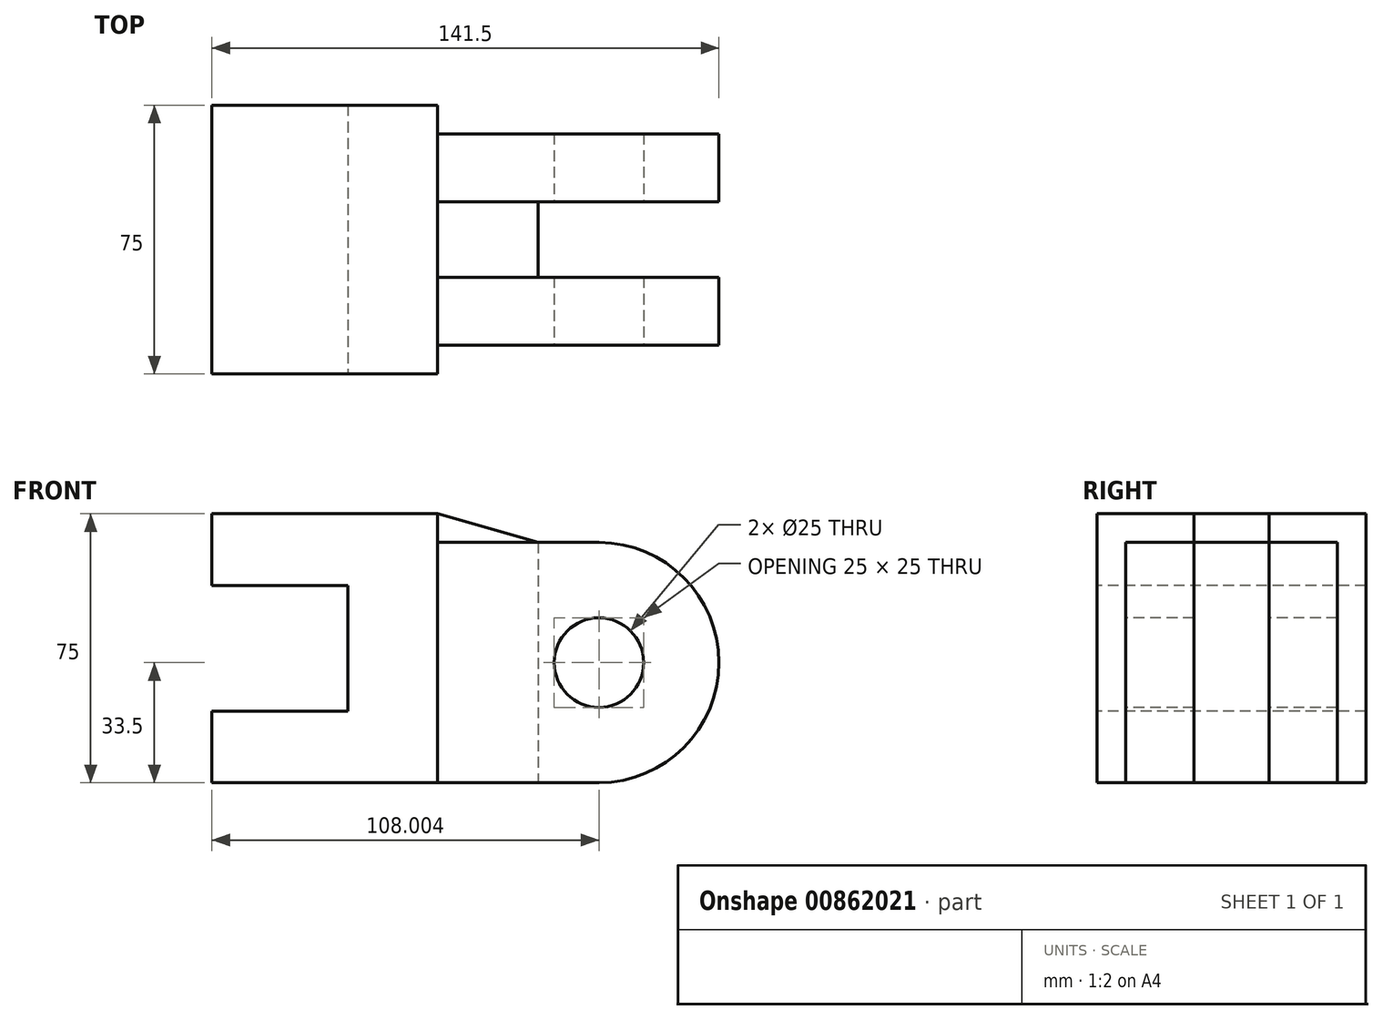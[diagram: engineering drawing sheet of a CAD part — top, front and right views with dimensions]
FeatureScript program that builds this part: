
annotation { "Feature Type Name" : "Feature", "Feature Type Description" : "" }
export const myFeature = defineFeature(function(context is Context, id is Id, definition is map)
    precondition{}
    {
        {
            var Q0;
            Q0=qCreatedBy(makeId("Top.planeOp"),FACE);
            var sketch = newSketch(context, id + "F0", { "sketchPlane" : qUnion([Q0])});
            skLineSegment(sketch, "E0.bottom", {"start": v(-50.72, 36.49) * mm, "end": v(12.28, 36.49) * mm});
            skLineSegment(sketch, "E0.top", {"start": v(-50.72, -38.51) * mm, "end": v(12.28, -38.51) * mm});
            skLineSegment(sketch, "E0.left", {"start": v(-50.72, 36.49) * mm, "end": v(-50.72, -38.51) * mm});
            skLineSegment(sketch, "E0.right", {"start": v(12.28, 36.49) * mm, "end": v(12.28, -38.51) * mm});
            skSolve(sketch);
        }
        {
            var Q0;
            Q0=qSketchRegion(id+"F0",true);
            extrude(context, id + "F1", {"entities" : qUnion([Q0]), "depth" : 75 * mm, "offsetDistance" : 25 * mm});
        }
        {
            var Q0;
            Q0=makeQuery(id+"F1.opExtrude","SWEPT_FACE",FACE,{"disambiguationData":[OSD([sQuery(id+"F0.wireOp",EDGE,"E0.top")])]});
            var sketch = newSketch(context, id + "F2", { "sketchPlane" : qUnion([Q0])});
            skLineSegment(sketch, "E1", {"start": v(-50.72, 0) * mm, "end": v(-50.72, 20) * mm});
            skLineSegment(sketch, "E2", {"start": v(-50.72, 20) * mm, "end": v(-12.72, 20) * mm});
            skLineSegment(sketch, "E3", {"start": v(-12.72, 20) * mm, "end": v(-12.72, 55) * mm});
            skLineSegment(sketch, "E4", {"start": v(-12.72, 55) * mm, "end": v(-50.72, 55) * mm});
            skLineSegment(sketch, "E5", {"start": v(-50.72, 55) * mm, "end": v(-50.72, 75) * mm});
            skSolve(sketch);
        }
        {
            var Q0;
            {var subQ0=sQuery(id+"F2.wireOp",EDGE,"E2");Q0=makeQuery(id+"F2.imprint","IMPRINT",FACE,{"disambiguationData":[TD([[makeQuery(id+"F2.imprint","IMPRINT",EDGE,{"derivedFrom":subQ0}),1.0]])]});}
            extrude(context, id + "F3", {"entities" : qUnion([Q0]), "operationType" : NewBodyOperationType.REMOVE, "oppositeDirection" : true, "depth" : 75 * mm, "offsetDistance" : 25 * mm});
        }
        {
            var Q0;
            Q0=makeQuery(id+"F1.opExtrude","SWEPT_FACE",FACE,{"disambiguationData":[OSD([sQuery(id+"F0.wireOp",EDGE,"E0.right")])]});
            var sketch = newSketch(context, id + "F4", { "sketchPlane" : qUnion([Q0])});
            skLineSegment(sketch, "E6", {"start": v(-30.51, 67) * mm, "end": v(-30.51, 0) * mm});
            skLineSegment(sketch, "E7", {"start": v(-30.51, 0) * mm, "end": v(-11.51, 0) * mm});
            skLineSegment(sketch, "E8", {"start": v(-11.51, 0) * mm, "end": v(9.49, 0) * mm});
            skLineSegment(sketch, "E9", {"start": v(9.49, 0) * mm, "end": v(28.49, 0) * mm});
            skLineSegment(sketch, "E10", {"start": v(28.49, 0) * mm, "end": v(28.49, 67) * mm});
            skLineSegment(sketch, "E11", {"start": v(28.49, 67) * mm, "end": v(9.49, 67) * mm});
            skLineSegment(sketch, "E12", {"start": v(9.49, 67) * mm, "end": v(9.49, 0) * mm});
            skLineSegment(sketch, "E13", {"start": v(-30.51, 67) * mm, "end": v(-11.51, 67) * mm});
            skLineSegment(sketch, "E14", {"start": v(-11.51, 67) * mm, "end": v(-11.51, 0) * mm});
            skLineSegment(sketch, "E15", {"start": v(-11.51, 67) * mm, "end": v(-11.51, 75) * mm});
            skLineSegment(sketch, "E16", {"start": v(-11.51, 75) * mm, "end": v(9.49, 75) * mm});
            skLineSegment(sketch, "E17", {"start": v(9.49, 75) * mm, "end": v(9.49, 67) * mm});
            skSolve(sketch);
        }
        {
            var Q0;
            Q0=makeQuery(id+"F4.imprint","IMPRINT",FACE,{"disambiguationData":[TD([[makeQuery(id+"F4.imprint","IMPRINT",EDGE,{"derivedFrom":sQuery(id+"F4.wireOp",EDGE,"E6")}),1.0]])]});
            var Q1;
            Q1=makeQuery(id+"F4.imprint","IMPRINT",FACE,{"disambiguationData":[TD([[makeQuery(id+"F4.imprint","IMPRINT",EDGE,{"derivedFrom":sQuery(id+"F4.wireOp",EDGE,"E9")}),-1.0]])]});
            extrude(context, id + "F5", {"entities" : qUnion([Q0, Q1]), "operationType" : NewBodyOperationType.ADD, "depth" : 45 * mm, "offsetDistance" : 25 * mm});
        }
        {
            var Q0;
            Q0=makeQuery(id+"F1.opExtrude","SWEPT_FACE",FACE,{"disambiguationData":[OSD([sQuery(id+"F0.wireOp",EDGE,"E0.right")])]});
            var sketch = newSketch(context, id + "F6", { "sketchPlane" : qUnion([Q0])});
            skLineSegment(sketch, "E18", {"start": v(-11.51, 67) * mm, "end": v(-11.51, 75) * mm});
            skLineSegment(sketch, "E19", {"start": v(-11.51, 75) * mm, "end": v(9.49, 75) * mm});
            skLineSegment(sketch, "E20", {"start": v(9.49, 75) * mm, "end": v(9.49, 67) * mm});
            skLineSegment(sketch, "E21", {"start": v(9.49, 67) * mm, "end": v(9.49, 0) * mm});
            skLineSegment(sketch, "E22", {"start": v(9.49, 0) * mm, "end": v(-11.51, 0) * mm});
            skLineSegment(sketch, "E23", {"start": v(-11.51, 0) * mm, "end": v(-11.51, 67) * mm});
            skSolve(sketch);
        }
        {
            var Q0;
            Q0=makeQuery(id+"F6.imprint","IMPRINT",FACE,{"disambiguationData":[TD([[makeQuery(id+"F6.imprint","IMPRINT",EDGE,{"derivedFrom":sQuery(id+"F6.wireOp",EDGE,"E18")}),-1.0]])]});
            extrude(context, id + "F7", {"entities" : qUnion([Q0]), "operationType" : NewBodyOperationType.ADD, "depth" : 28 * mm, "offsetDistance" : 25 * mm});
        }
        {
            var Q0;
            Q0=makeQuery(id+"F7.opExtrude","SWEPT_FACE",FACE,{"disambiguationData":[OSD([sQuery(id+"F6.wireOp",EDGE,"E18"),sQuery(id+"F6.wireOp",EDGE,"E23")])]});
            var sketch = newSketch(context, id + "F8", { "sketchPlane" : qUnion([Q0])});
            skLineSegment(sketch, "E24", {"start": v(12.28, 75) * mm, "end": v(40.28, 67) * mm});
            skSolve(sketch);
        }
        {
            var Q0;
            Q0=makeQuery(id+"F8.imprint","IMPRINT",FACE,{"disambiguationData":[TD([[makeQuery(id+"F8.imprint","IMPRINT",EDGE,{"derivedFrom":sQuery(id+"F8.wireOp",EDGE,"E24")}),1.0]])]});
            extrude(context, id + "F9", {"entities" : qUnion([Q0]), "operationType" : NewBodyOperationType.REMOVE, "oppositeDirection" : true, "depth" : 25 * mm, "offsetDistance" : 25 * mm});
        }
        {
            var Q0;
            Q0=makeQuery(id+"F5.opExtrude","SWEPT_FACE",FACE,{"disambiguationData":[OSD([sQuery(id+"F4.wireOp",EDGE,"E6")])]});
            var sketch = newSketch(context, id + "F10", { "sketchPlane" : qUnion([Q0])});
            skArc(sketch, "E25", {"start": v(57.28, 0) * mm, "mid": v(90.78, 33.5) * mm, "end": v(57.28, 67) * mm});
            skSolve(sketch);
        }
        {
            var Q0;
            Q0=makeQuery(id+"F10.imprint","IMPRINT",FACE,{"disambiguationData":[TD([[makeQuery(id+"F10.imprint","IMPRINT",EDGE,{"derivedFrom":sQuery(id+"F10.wireOp",EDGE,"E25")}),1.0]])]});
            extrude(context, id + "F11", {"entities" : qUnion([Q0]), "operationType" : NewBodyOperationType.ADD, "oppositeDirection" : true, "depth" : 19 * mm, "offsetDistance" : 25 * mm});
        }
        {
            var Q0;
            Q0=makeQuery(id+"F5.opExtrude","SWEPT_FACE",FACE,{"disambiguationData":[OSD([sQuery(id+"F4.wireOp",EDGE,"E10")])]});
            var sketch = newSketch(context, id + "F12", { "sketchPlane" : qUnion([Q0])});
            skArc(sketch, "E26", {"start": v(-57.28, 67) * mm, "mid": v(-90.78, 33.5) * mm, "end": v(-57.28, 0) * mm});
            skSolve(sketch);
        }
        {
            var Q0;
            Q0=makeQuery(id+"F12.imprint","IMPRINT",FACE,{"disambiguationData":[TD([[makeQuery(id+"F12.imprint","IMPRINT",EDGE,{"derivedFrom":sQuery(id+"F12.wireOp",EDGE,"E26")}),1.0]])]});
            extrude(context, id + "F13", {"entities" : qUnion([Q0]), "operationType" : NewBodyOperationType.ADD, "oppositeDirection" : true, "depth" : 19 * mm, "offsetDistance" : 25 * mm});
        }
        {
            var Q0;
            {var subQ0=sQuery(id+"F4.wireOp",EDGE,"E6");Q0=makeQuery(id+"F11.boolean.opBoolean","MERGE",FACE,{"derivedFrom":[makeQuery(id+"F5.opExtrude","SWEPT_FACE",FACE,{"disambiguationData":[OSD([subQ0])]}),makeQuery(id+"F11.opExtrude","CAP_FACE",FACE,{"disambiguationData":[OSD([subQ0,sQuery(id+"F10.wireOp",EDGE,"E25")])],"isStart":true})]});}
            var sketch = newSketch(context, id + "F14", { "sketchPlane" : qUnion([Q0])});
            skLineSegment(sketch, "E27", {"start": v(12.28, 67) * mm, "end": v(57.28, 67) * mm});
            skLineSegment(sketch, "E28", {"start": v(57.28, 67) * mm, "end": v(57.28, 33.5) * mm});
            skCircle(sketch, "E29", {"center": v(57.28, 33.5) * mm, "radius": 12.5 * mm});
            skSolve(sketch);
        }
        {
            var Q0;
            Q0=makeQuery(id+"F14.imprint","IMPRINT",FACE,{"disambiguationData":[TD([[makeQuery(id+"F14.imprint","IMPRINT",EDGE,{"derivedFrom":sQuery(id+"F14.wireOp",EDGE,"E29")}),1.0]])]});
            extrude(context, id + "F15", {"entities" : qUnion([Q0]), "operationType" : NewBodyOperationType.REMOVE, "oppositeDirection" : true, "depth" : 100 * mm, "offsetDistance" : 25 * mm});
        }
    });
